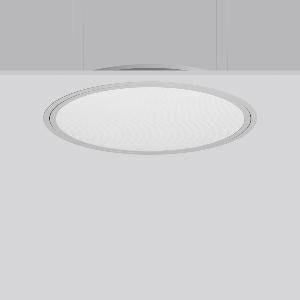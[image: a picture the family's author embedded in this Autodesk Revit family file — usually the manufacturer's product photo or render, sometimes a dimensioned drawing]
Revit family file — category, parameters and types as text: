
# Revit family: triona_round_e_312296_004_2_12_1ec1
name_source: partatom
category: Lighting Fixtures
units: mm (PartAtom-declared; Revit-internal decimal feet)

## family parameters
Cut with Voids When Loaded = No
Host = Face
Light Source = No
Part Type = Normal
Room Calculation Point = No
Round Connector Dimension = Use Diameter
Shared = No

## types (1)
- TuneableWhite 846 (1 x LED Modul 846, 3550 lm, 4600)
    Apparent Load = 40 VA
    CIE Flux Codes = 59 87 97 100 100
    Color Rendering = 80
    Color Temperature = 4600
    Default Elevation = 1800 mm
    Description = Series: TRIONA round
Decorative round LED recessed surface luminaire. Cover made of sheet steel, powder-coated. Frame made of aluminium, powder-coated. Recessed ring: aluminium extrusion profile, powder coated. Light emission through a diffuser in plastic, opal/prismatic. Lightguide and diffuser made of non-yellowing plastic (PMMA). Lateral light emission (RZB SIDELITE technology) for above-average homogeneous light distribution. Tunable white versions, dynamically adjustable from 2700 K to 6500 K. Suitable for installation in cavity ceilings. Tool-free mounting system thanks to the rocker arm mechanism (patent pending). Electronic ballast included. Very easy installation thanks to Plug+Play connection. Ideal for use as part of the Human Centric Lighting concept in connection with RZB light management systems. 
Colour: silver, matt (approx. RAL 9006)
Diameter: 725 mm
Height: 2 mm
Cut-out diameter: 702 mm
Recess height: 100 mm
Luminaire: recess height: 89 mm
Lamp: LED
Socket: without socket
Colour temperature: 2700K - 6500K
Colour rendering index (CRI): 80
System power: 40 W
Rated luminous flux: 3550 lm
Luminous efficiency: 89 lm/W
System power 2: 42 W
Rated luminous flux 2: 3400 lm
Luminous efficiency 2: 81 lm/W
System power 3: 42 W
Rated luminous flux 3: 3400 lm
Luminous efficiency 3: 81 lm/W
Control gear: Converter, dimmable, DALI
Protection class: I
Type of protection: IP 40
    Height = 0 mm  [stored 0 ft]
    Lamp = 1 x LED Modul 846
    Lamp Light Flux = 3550 lm
    Lamp count = 1
    Length = 725 mm
    Lifetime = 50000 h
    Luminous efficacy = 89 lm/W
    Manufacturer = RZB
    ModVariant = No
    Model = 312296.004.2.12
    Mounting Place = Ceiling
    Mounting Type = Recessed
    Number of Poles = 1
    OnlyDefault = Yes
    Power Factor = 1
    Product Name = TRIONA round E
    Product group = Recessed modular luminaires
    ProductGroupID = 406
    Protection Class = Protection class I
    Protection Degree = IP 20
    RLX_Detail_Level = 1
    RLX_Emergency_Light_Flux = 0 lm
    RLX_Emergency_Type = 0
    RLX_Emergency_Type_DB = No
    RlxData = <blob elided: 37841 chars, md5=287cfb74>
    Socket = socket
    Standby Power = 0 W
    System Light Flux = 3550 lm
    System Power = 40 W
    Type Comments = TuneableWhite 846
    Type Image = 312296.004.12.jpg
    URL = http://relux.com
    VarID = tuneablewhite_846
    Voltage = 230 V
    Voltage Range = 220-240 V
    Weight = 0.00 kg
    Width = 0 mm  [stored 0 ft]

note: [stored X ft] marks values corroborated as IEEE doubles in the binary element streams (Revit-internal decimal feet)

## geometry (parser evidence)
native form markers: Blend x4, Sweep x11
no freeform markers — native parametric forms only
